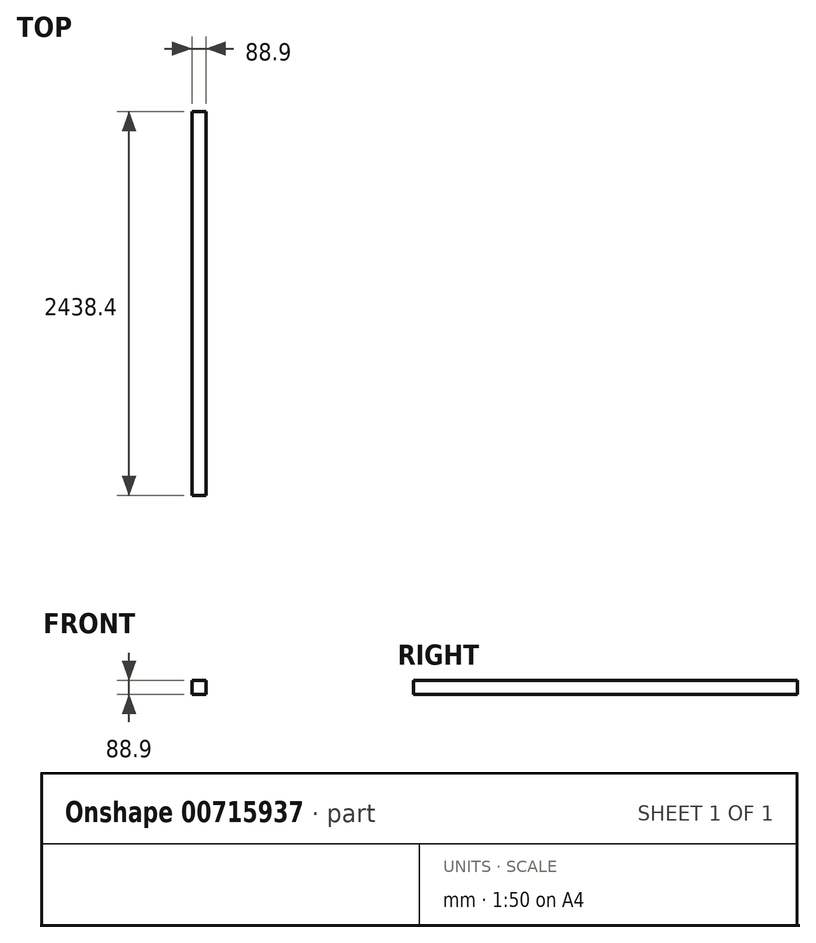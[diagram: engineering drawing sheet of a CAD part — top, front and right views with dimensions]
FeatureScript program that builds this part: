
annotation { "Feature Type Name" : "Feature", "Feature Type Description" : "" }
export const myFeature = defineFeature(function(context is Context, id is Id, definition is map)
    precondition{}
    {
        {
            var Q0;
            Q0=qCreatedBy(makeId("Front.planeOp"),FACE);
            var sketch = newSketch(context, id + "F0", { "sketchPlane" : qUnion([Q0])});
            skLineSegment(sketch, "E0.bottom", {"start": v(-44.45, 44.45) * mm, "end": v(44.45, 44.45) * mm});
            skLineSegment(sketch, "E0.top", {"start": v(-44.45, -44.45) * mm, "end": v(44.45, -44.45) * mm});
            skLineSegment(sketch, "E0.left", {"start": v(-44.45, 44.45) * mm, "end": v(-44.45, -44.45) * mm});
            skLineSegment(sketch, "E0.right", {"start": v(44.45, 44.45) * mm, "end": v(44.45, -44.45) * mm});
            skPoint(sketch, "E0.middle", {"position": v(0, 0) * mm});
            skSolve(sketch);
        }
        {
            var Q0;
            Q0=makeQuery(id+"F0.imprint","IMPRINT",FACE,{"disambiguationData":[TD([[makeQuery(id+"F0.imprint","IMPRINT",EDGE,{"derivedFrom":sQuery(id+"F0.wireOp",EDGE,"E0.bottom")}),-1.0]])]});
            extrude(context, id + "F1", {"entities" : qUnion([Q0]), "endBound" : BoundingType.SYMMETRIC, "depth" : 2438.4 * mm, "offsetDistance" : 25.4 * mm});
        }
    });
